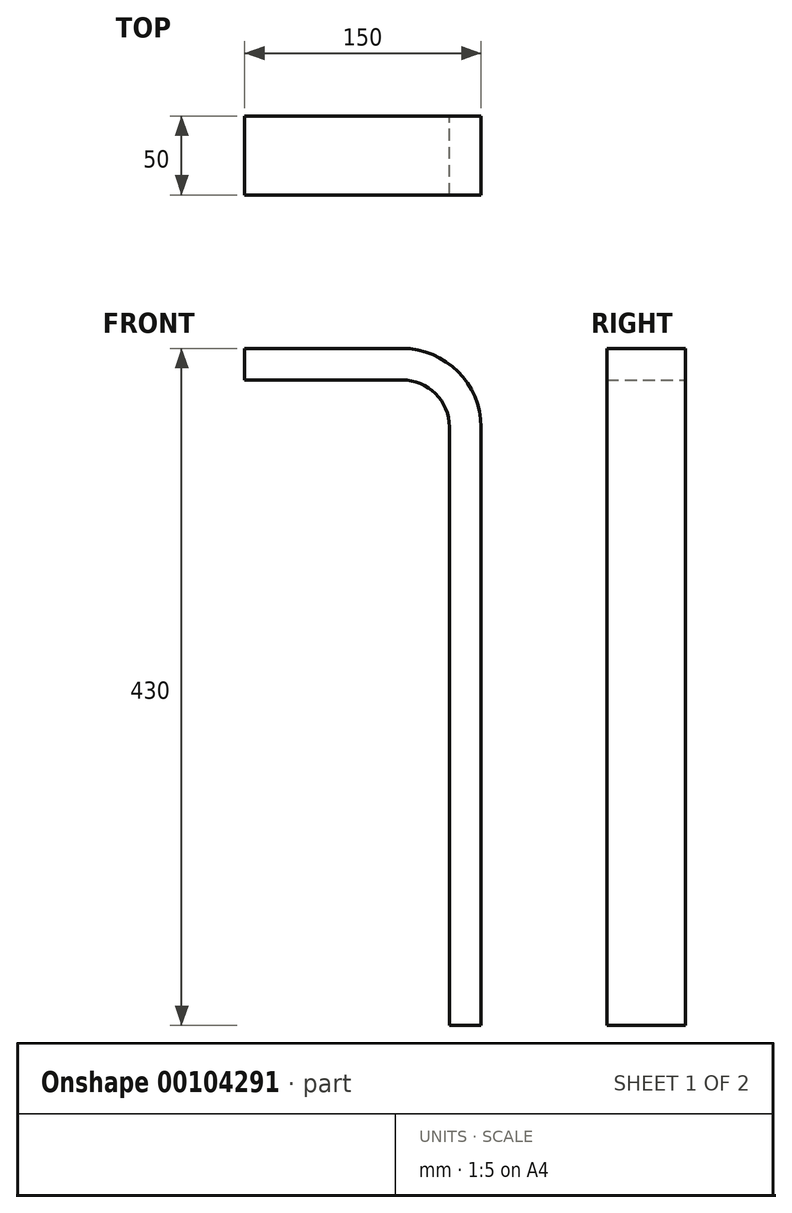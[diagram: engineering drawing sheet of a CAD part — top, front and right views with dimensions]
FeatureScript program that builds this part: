
annotation { "Feature Type Name" : "Feature", "Feature Type Description" : "" }
export const myFeature = defineFeature(function(context is Context, id is Id, definition is map)
    precondition{}
    {
        {
            var Q0;
            Q0=qCreatedBy(makeId("Front.planeOp"),FACE);
            var sketch = newSketch(context, id + "F0", { "sketchPlane" : qUnion([Q0])});
            skLineSegment(sketch, "E0", {"start": v(0, 0) * mm, "end": v(100, 0) * mm});
            skLineSegment(sketch, "E1", {"start": v(150, -50) * mm, "end": v(150, -430) * mm});
            skPoint(sketch, "E2.visualSharp", {"position": v(150, 0) * mm});
            skArc(sketch, "E2.filletArc", {"start": v(150, -50) * mm, "mid": v(135.36, -14.64) * mm, "end": v(100, 0) * mm});
            skLineSegment(sketch, "E3.0", {"start": v(130, -50) * mm, "end": v(130, -430) * mm});
            skArc(sketch, "E3.1", {"start": v(130, -50) * mm, "mid": v(121.21, -28.79) * mm, "end": v(100, -20) * mm});
            skLineSegment(sketch, "E3.2", {"start": v(0, -20) * mm, "end": v(100, -20) * mm});
            skLineSegment(sketch, "E4", {"start": v(0, -20) * mm, "end": v(0, 0) * mm});
            skLineSegment(sketch, "E5", {"start": v(130, -430) * mm, "end": v(150, -430) * mm});
            skSolve(sketch);
        }
        {
            var Q0;
            Q0=makeQuery(id+"F0.imprint","IMPRINT",FACE,{"disambiguationData":[TD([[makeQuery(id+"F0.imprint","IMPRINT",EDGE,{"derivedFrom":sQuery(id+"F0.wireOp",EDGE,"E0")}),-1.0]])]});
            extrude(context, id + "F1", {"entities" : qUnion([Q0]), "depth" : 25 * mm, "hasSecondDirection" : true, "secondDirectionOppositeDirection" : true, "secondDirectionDepth" : 25 * mm});
        }
    });
